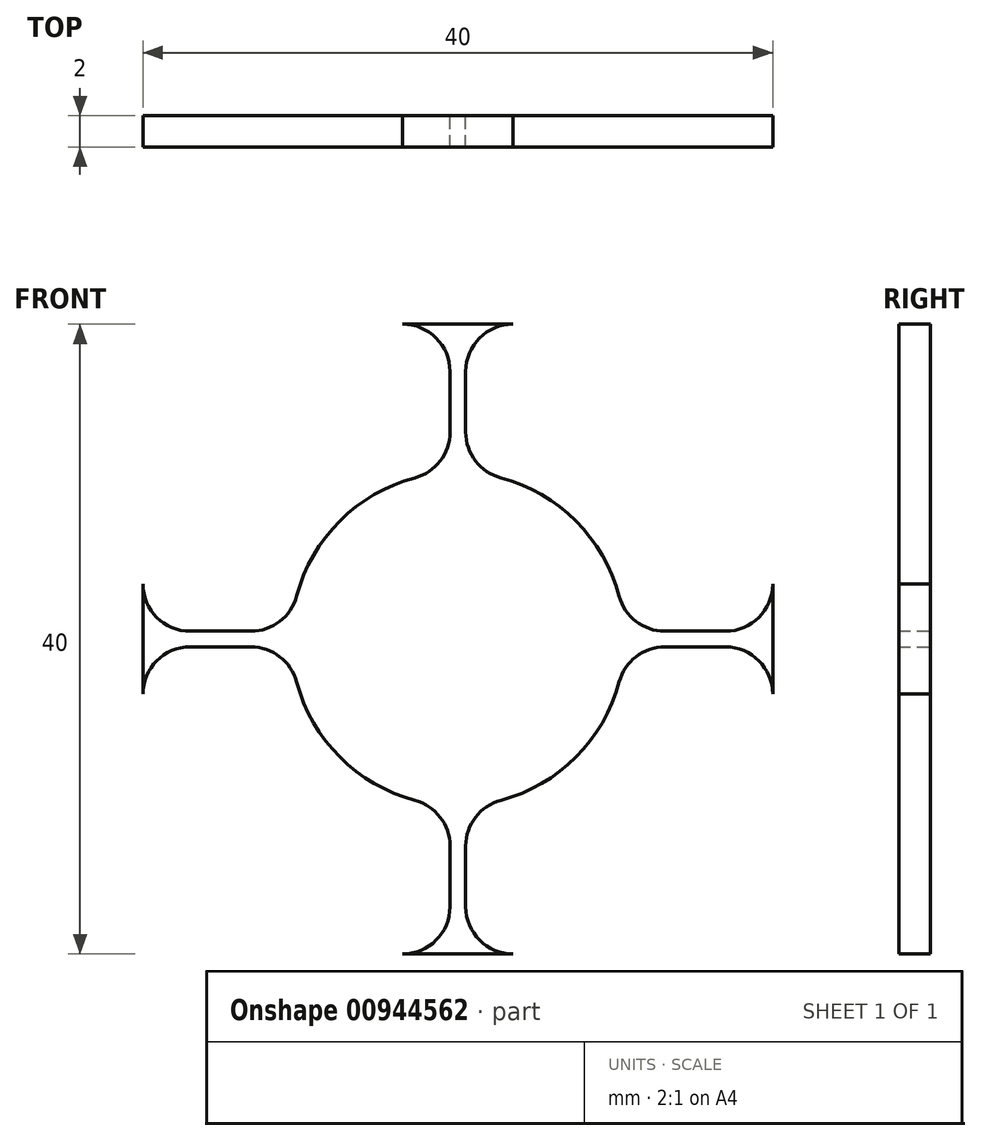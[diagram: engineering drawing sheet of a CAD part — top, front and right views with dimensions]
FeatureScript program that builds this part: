
annotation { "Feature Type Name" : "Feature", "Feature Type Description" : "" }
export const myFeature = defineFeature(function(context is Context, id is Id, definition is map)
    precondition{}
    {
        {
            var Q0;
            Q0=qCreatedBy(makeId("Front.planeOp"),FACE);
            var sketch = newSketch(context, id + "F0", { "sketchPlane" : qUnion([Q0])});
            skArc(sketch, "E0", {"start": v(-10.24, -2.73) * mm, "mid": v(-7.5, -7.5) * mm, "end": v(-2.73, -10.24) * mm});
            skLineSegment(sketch, "E1", {"start": v(0, 0) * mm, "end": v(0, 25.04) * mm});
            skPoint(sketch, "E1.endSnap0", {"position": v(0, 20) * mm});
            skLineSegment(sketch, "E2", {"start": v(0, 25.04) * mm, "end": v(0, -26.03) * mm, "construction": true});
            skLineSegment(sketch, "E3", {"start": v(0, 0) * mm, "end": v(24.93, 0) * mm});
            skLineSegment(sketch, "E4", {"start": v(24.93, 0) * mm, "end": v(0, 0) * mm, "construction": true});
            skLineSegment(sketch, "E5.bottom", {"start": v(17, -0.5) * mm, "end": v(13.14, -0.5) * mm});
            skLineSegment(sketch, "E5.top", {"start": v(17, 0.5) * mm, "end": v(13.14, 0.5) * mm});
            skPoint(sketch, "E5.middle", {"position": v(13.5, 0) * mm});
            skLineSegment(sketch, "E6.left", {"start": v(0.5, 17) * mm, "end": v(0.5, 13.14) * mm});
            skLineSegment(sketch, "E6.right", {"start": v(-0.5, 17) * mm, "end": v(-0.5, 13.14) * mm});
            skPoint(sketch, "E6.middle", {"position": v(0, 12.52) * mm});
            skLineSegment(sketch, "E7.bottom", {"start": v(-17, -0.5) * mm, "end": v(-13.14, -0.5) * mm});
            skLineSegment(sketch, "E7.top", {"start": v(-17, 0.5) * mm, "end": v(-13.14, 0.5) * mm});
            skPoint(sketch, "E7.middle", {"position": v(-13.5, 0) * mm});
            skLineSegment(sketch, "E8.left", {"start": v(0.5, -17) * mm, "end": v(0.5, -13.14) * mm});
            skLineSegment(sketch, "E8.right", {"start": v(-0.5, -17) * mm, "end": v(-0.5, -13.14) * mm});
            skPoint(sketch, "E8.middle", {"position": v(0, -14.07) * mm});
            skLineSegment(sketch, "E9.trimOffspring", {"start": v(-10.6, 0) * mm, "end": v(-28.78, 0) * mm, "construction": true});
            skPoint(sketch, "E10.orphan", {"position": v(-6.98, 0.5) * mm});
            skPoint(sketch, "E7.right.start.orphan", {"position": v(-6.98, -0.5) * mm});
            skPoint(sketch, "E11.orphan", {"position": v(-0.5, -8.13) * mm});
            skPoint(sketch, "E12.orphan", {"position": v(0.5, -8.13) * mm});
            skPoint(sketch, "E13.orphan", {"position": v(7.01, 0.5) * mm});
            skPoint(sketch, "E14.orphan", {"position": v(7.01, -0.5) * mm});
            skPoint(sketch, "E15.orphan", {"position": v(0.5, 5.04) * mm});
            skPoint(sketch, "E16.orphan", {"position": v(-0.5, 5.04) * mm});
            skArc(sketch, "E17.trimOffspring", {"start": v(-2.73, 10.24) * mm, "mid": v(-7.5, 7.5) * mm, "end": v(-10.24, 2.73) * mm});
            skArc(sketch, "E18.trimOffspring", {"start": v(10.24, 2.73) * mm, "mid": v(7.5, 7.5) * mm, "end": v(2.73, 10.24) * mm});
            skArc(sketch, "E19.trimOffspring", {"start": v(2.73, -10.24) * mm, "mid": v(7.5, -7.5) * mm, "end": v(10.24, -2.73) * mm});
            skPoint(sketch, "E20.visualSharp", {"position": v(-0.5, 10.59) * mm});
            skArc(sketch, "E20.filletArc", {"start": v(-2.73, 10.24) * mm, "mid": v(-1.12, 11.31) * mm, "end": v(-0.5, 13.14) * mm});
            skPoint(sketch, "E21.visualSharp", {"position": v(0.5, 10.59) * mm});
            skArc(sketch, "E21.filletArc", {"start": v(0.5, 13.14) * mm, "mid": v(1.12, 11.31) * mm, "end": v(2.73, 10.24) * mm});
            skPoint(sketch, "E22.visualSharp", {"position": v(10.59, 0.5) * mm});
            skArc(sketch, "E22.filletArc", {"start": v(10.24, 2.73) * mm, "mid": v(11.31, 1.12) * mm, "end": v(13.14, 0.5) * mm});
            skPoint(sketch, "E23.visualSharp", {"position": v(10.59, -0.5) * mm});
            skArc(sketch, "E23.filletArc", {"start": v(13.14, -0.5) * mm, "mid": v(11.31, -1.12) * mm, "end": v(10.24, -2.73) * mm});
            skPoint(sketch, "E24.visualSharp", {"position": v(0.5, -10.59) * mm});
            skArc(sketch, "E24.filletArc", {"start": v(2.73, -10.24) * mm, "mid": v(1.12, -11.31) * mm, "end": v(0.5, -13.14) * mm});
            skPoint(sketch, "E25.visualSharp", {"position": v(-0.5, -10.59) * mm});
            skArc(sketch, "E25.filletArc", {"start": v(-0.5, -13.14) * mm, "mid": v(-1.12, -11.31) * mm, "end": v(-2.73, -10.24) * mm});
            skPoint(sketch, "E26.visualSharp", {"position": v(-10.59, -0.5) * mm});
            skArc(sketch, "E26.filletArc", {"start": v(-10.24, -2.73) * mm, "mid": v(-11.31, -1.12) * mm, "end": v(-13.14, -0.5) * mm});
            skPoint(sketch, "E27.visualSharp", {"position": v(-10.59, 0.5) * mm});
            skArc(sketch, "E27.filletArc", {"start": v(-13.14, 0.5) * mm, "mid": v(-11.31, 1.12) * mm, "end": v(-10.24, 2.73) * mm});
            skPoint(sketch, "E28.visualSharp", {"position": v(20, -0.5) * mm});
            skArc(sketch, "E28.filletArc", {"start": v(20, -3.5) * mm, "mid": v(19.12, -1.38) * mm, "end": v(17, -0.5) * mm});
            skPoint(sketch, "E29.visualSharp", {"position": v(20, 0.5) * mm});
            skArc(sketch, "E29.filletArc", {"start": v(17, 0.5) * mm, "mid": v(19.12, 1.38) * mm, "end": v(20, 3.5) * mm});
            skLineSegment(sketch, "E30", {"start": v(20, -3.5) * mm, "end": v(20, 3.5) * mm});
            skPoint(sketch, "E31.visualSharp", {"position": v(-0.5, 20) * mm});
            skArc(sketch, "E31.filletArc", {"start": v(-0.5, 17) * mm, "mid": v(-1.38, 19.12) * mm, "end": v(-3.5, 20) * mm});
            skPoint(sketch, "E32.visualSharp", {"position": v(0.5, 20) * mm});
            skArc(sketch, "E32.filletArc", {"start": v(3.5, 20) * mm, "mid": v(1.38, 19.12) * mm, "end": v(0.5, 17) * mm});
            skPoint(sketch, "E33.visualSharp", {"position": v(-20, 0.5) * mm});
            skArc(sketch, "E33.filletArc", {"start": v(-20, 3.5) * mm, "mid": v(-19.12, 1.38) * mm, "end": v(-17, 0.5) * mm});
            skPoint(sketch, "E34.visualSharp", {"position": v(-20, -0.5) * mm});
            skArc(sketch, "E34.filletArc", {"start": v(-17, -0.5) * mm, "mid": v(-19.12, -1.38) * mm, "end": v(-20, -3.5) * mm});
            skPoint(sketch, "E35.visualSharp", {"position": v(-0.5, -20) * mm});
            skArc(sketch, "E35.filletArc", {"start": v(-3.5, -20) * mm, "mid": v(-1.38, -19.12) * mm, "end": v(-0.5, -17) * mm});
            skPoint(sketch, "E36.visualSharp", {"position": v(0.5, -20) * mm});
            skArc(sketch, "E36.filletArc", {"start": v(0.5, -17) * mm, "mid": v(1.38, -19.12) * mm, "end": v(3.5, -20) * mm});
            skLineSegment(sketch, "E37", {"start": v(-3.5, -20) * mm, "end": v(3.5, -20) * mm});
            skLineSegment(sketch, "E38", {"start": v(-20, -3.5) * mm, "end": v(-20, 3.5) * mm});
            skLineSegment(sketch, "E39", {"start": v(-3.5, 20) * mm, "end": v(3.5, 20) * mm});
            skPoint(sketch, "E40.orphan", {"position": v(17, -17) * mm});
            skPoint(sketch, "E41.left.start.orphan", {"position": v(20, -20) * mm});
            skPoint(sketch, "E41.right.start.orphan", {"position": v(-20, -20) * mm});
            skPoint(sketch, "E42.orphan", {"position": v(-17, -17) * mm});
            skPoint(sketch, "E43.trimOffspring.end.orphan", {"position": v(-20, 20) * mm});
            skPoint(sketch, "E44.orphan", {"position": v(-17, 17) * mm});
            skPoint(sketch, "E45.orphan", {"position": v(17, 17) * mm});
            skPoint(sketch, "E41.top.start.orphan", {"position": v(20, 20) * mm});
            skSolve(sketch);
        }
        {
            var Q0;
            Q0 = qSketchRegion(id + "F0", true);
            extrude(context, id + "F1", {"entities" : qUnion([Q0]), "depth" : 2 * mm, "offsetDistance" : 25 * mm});
        }
    });
